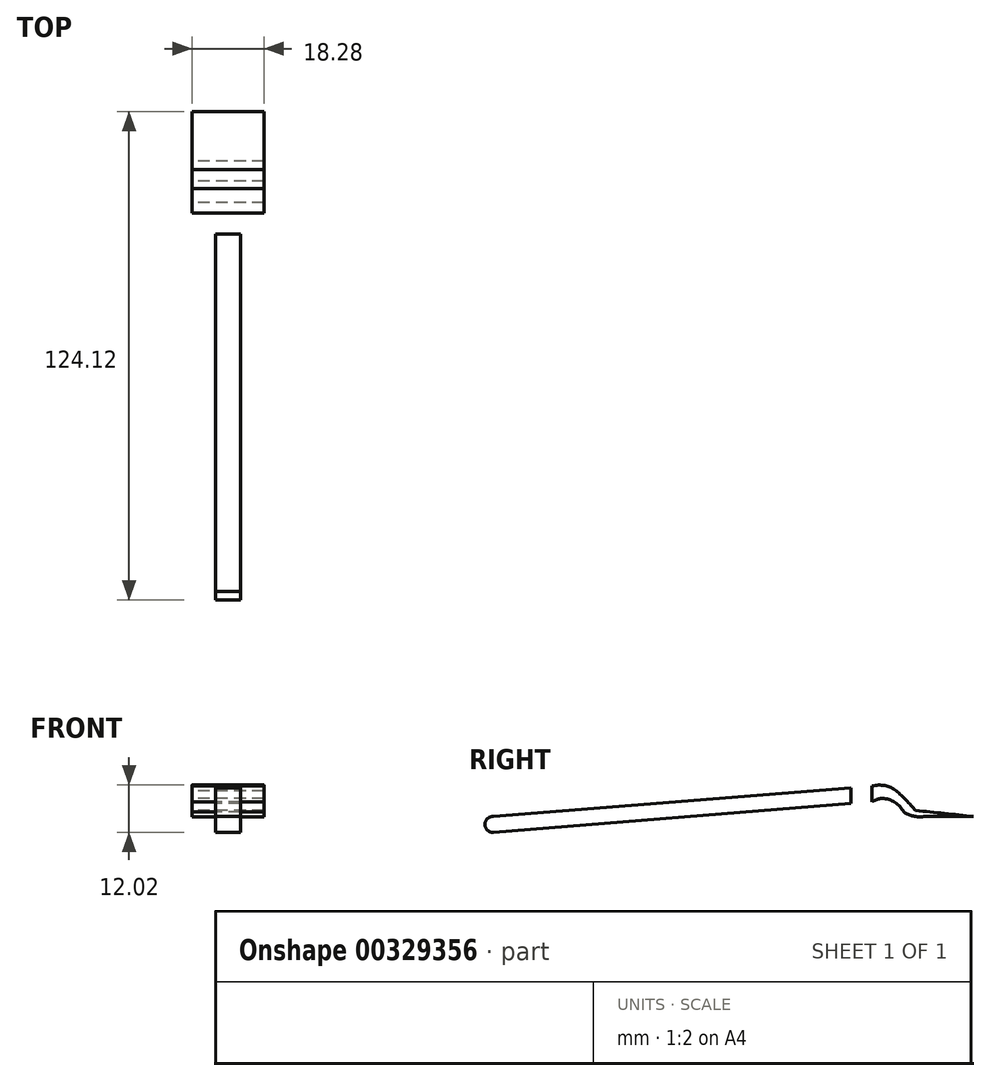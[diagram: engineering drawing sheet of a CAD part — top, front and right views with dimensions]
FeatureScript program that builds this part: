
annotation { "Feature Type Name" : "Feature", "Feature Type Description" : "" }
export const myFeature = defineFeature(function(context is Context, id is Id, definition is map)
    precondition{}
    {
        {
            var Q0;
            Q0=qCreatedBy(makeId("Right.planeOp"),FACE);
            var sketch = newSketch(context, id + "F0", { "sketchPlane" : qUnion([Q0])});
            skLineSegment(sketch, "E0", {"start": v(-96.2, 0) * mm, "end": v(0, 7.75) * mm});
            skLineSegment(sketch, "E1", {"start": v(-96.2, -4) * mm, "end": v(0, 3.74) * mm});
            skPoint(sketch, "E2", {"position": v(2.96, 7.91) * mm});
            skPoint(sketch, "E3", {"position": v(6.14, 6.56) * mm});
            skPoint(sketch, "E4", {"position": v(8.47, 4.36) * mm});
            skPoint(sketch, "E5", {"position": v(11.04, 1.54) * mm});
            skPoint(sketch, "E6", {"position": v(16.25, 1) * mm});
            skPoint(sketch, "E7", {"position": v(25.74, 0) * mm});
            skArc(sketch, "E8", {"start": v(6.14, 6.56) * mm, "mid": v(3.2, 7.87) * mm, "end": v(0, 7.75) * mm});
            skArc(sketch, "E9", {"start": v(11.04, 1.54) * mm, "mid": v(8.68, 4.14) * mm, "end": v(6.14, 6.56) * mm});
            skArc(sketch, "E10", {"start": v(11.04, 1.54) * mm, "mid": v(18.4, 0.78) * mm, "end": v(25.74, 0) * mm});
            skPoint(sketch, "E11", {"position": v(2.59, 4.6) * mm});
            skPoint(sketch, "E12", {"position": v(8.02, 1.14) * mm});
            skPoint(sketch, "E13", {"position": v(15.93, 0) * mm});
            skPoint(sketch, "E14", {"position": v(5.49, 3.78) * mm});
            skPoint(sketch, "E15", {"position": v(13.15, 0) * mm});
            skArc(sketch, "E16", {"start": v(5.49, 3.78) * mm, "mid": v(2.74, 4.6) * mm, "end": v(0, 3.74) * mm});
            skArc(sketch, "E17", {"start": v(8.02, 1.14) * mm, "mid": v(5.77, 3.6) * mm, "end": v(2.59, 4.6) * mm});
            skArc(sketch, "E18", {"start": v(8.02, 1.14) * mm, "mid": v(10.48, 0.12) * mm, "end": v(13.15, 0) * mm});
            skLineSegment(sketch, "E19", {"start": v(13.15, 0) * mm, "end": v(15.93, 0) * mm});
            skLineSegment(sketch, "E20", {"start": v(15.93, 0) * mm, "end": v(25.74, 0) * mm});
            skArc(sketch, "E21", {"start": v(-96.2, 0) * mm, "mid": v(-98.38, -2) * mm, "end": v(-96.2, -4) * mm});
            skLineSegment(sketch, "E22", {"start": v(0, 7.75) * mm, "end": v(0, 3.74) * mm});
            skLineSegment(sketch, "E23", {"start": v(-5.4, 7.31) * mm, "end": v(-5.32, 3.31) * mm});
            skSolve(sketch);
        }
        {
            var Q0;
            {var subQ0=sQuery(id+"F0.wireOp",EDGE,"E21");Q0=makeQuery(id+"F0.imprint","IMPRINT",FACE,{"disambiguationData":[TD([[makeQuery(id+"F0.imprint","IMPRINT",EDGE,{"derivedFrom":subQ0}),1.0]])]});}
            extrude(context, id + "F1", {"entities" : qUnion([Q0]), "depth" : 3.15 * mm, "hasSecondDirection" : true, "secondDirectionOppositeDirection" : true, "secondDirectionDepth" : 3.15 * mm});
        }
        {
            var Q0;
            {var subQ0=sQuery(id+"F0.wireOp",EDGE,"E17");var subQ1=sQuery(id+"F0.wireOp",EDGE,"E16");var subQ2=makeQuery(id+"F0.imprint","INTERSECT",VERTEX,{"disambiguationData":[OD(0.0)],"derivedFrom":[subQ1,subQ0]});Q0=makeQuery(id+"F0.imprint","IMPRINT",FACE,{"disambiguationData":[TD([[makeQuery(id+"F0.imprint","IMPRINT",EDGE,{"disambiguationData":[TD([[subQ2,-1.0]])],"derivedFrom":subQ1}),1.0]])]});}
            var Q1;
            Q1=makeQuery(id+"F0.imprint","IMPRINT",FACE,{"disambiguationData":[TD([[makeQuery(id+"F0.imprint","IMPRINT",EDGE,{"derivedFrom":sQuery(id+"F0.wireOp",EDGE,"E8")}),1.0]])]});
            extrude(context, id + "F2", {"entities" : qUnion([Q0, Q1]), "depth" : 9.14 * mm, "hasSecondDirection" : true, "secondDirectionOppositeDirection" : true, "secondDirectionDepth" : 9.14 * mm});
        }
    });
